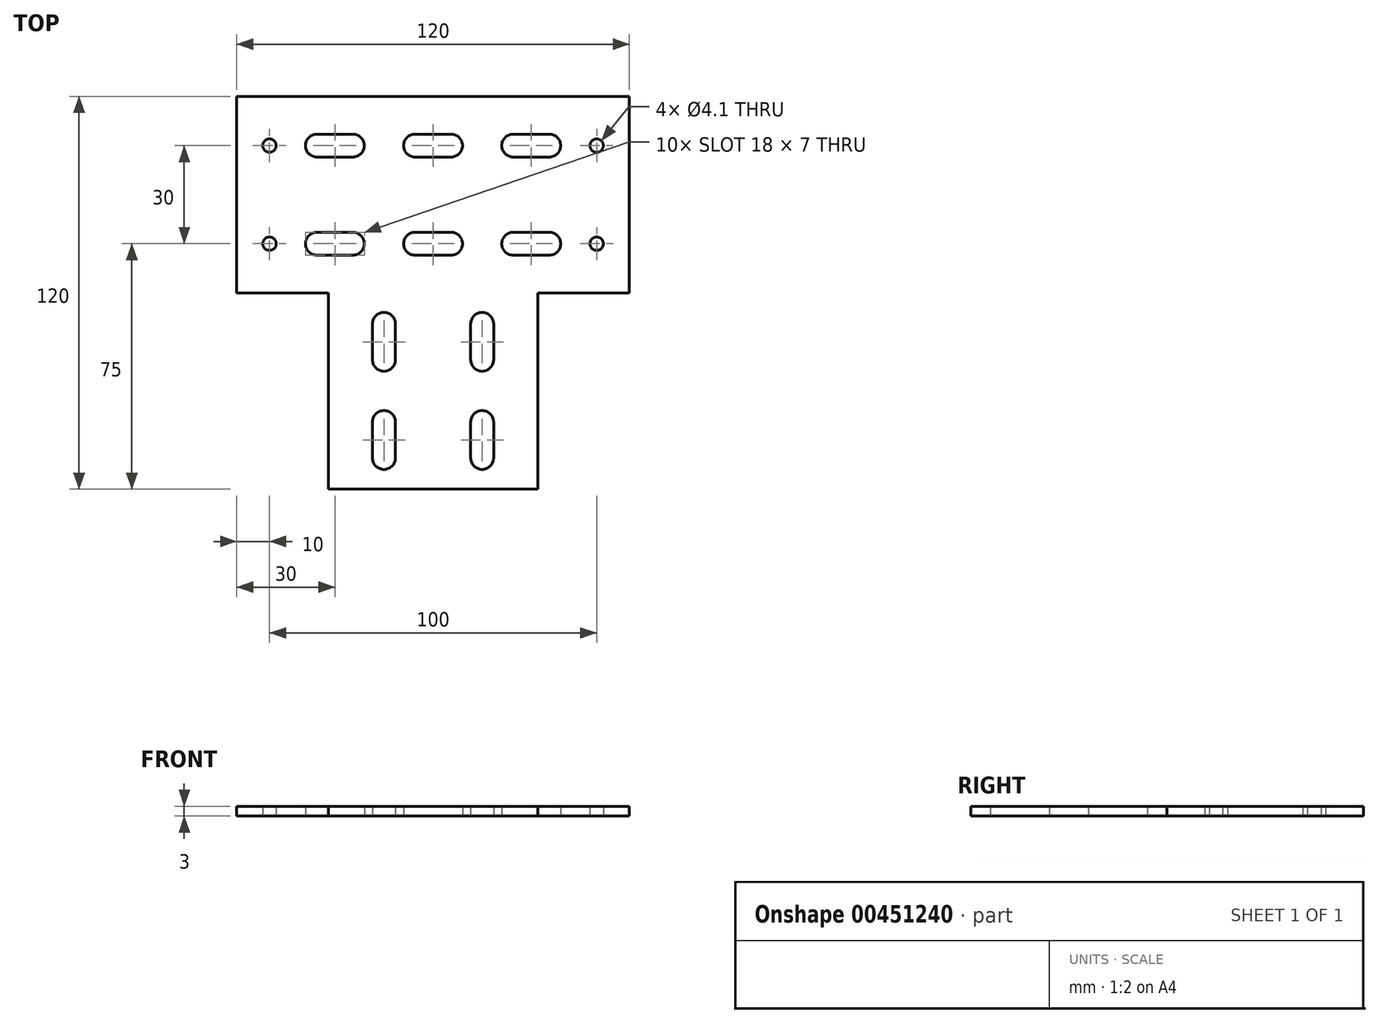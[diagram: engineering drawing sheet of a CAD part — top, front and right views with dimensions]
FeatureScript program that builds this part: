
annotation { "Feature Type Name" : "Feature", "Feature Type Description" : "" }
export const myFeature = defineFeature(function(context is Context, id is Id, definition is map)
    precondition{}
    {
        {
            var Q0;
            Q0=qCreatedBy(makeId("Top.planeOp"),FACE);
            var sketch = newSketch(context, id + "F0", { "sketchPlane" : qUnion([Q0])});
            skLineSegment(sketch, "E0.bottom", {"start": v(32, -60) * mm, "end": v(-32, -60) * mm});
            skLineSegment(sketch, "E0.left", {"start": v(32, -60) * mm, "end": v(32, 0) * mm});
            skLineSegment(sketch, "E0.right", {"start": v(-32, -60) * mm, "end": v(-32, 0) * mm});
            skPoint(sketch, "E0.middle", {"position": v(0, 0) * mm});
            skLineSegment(sketch, "E1", {"start": v(60, 60) * mm, "end": v(60, 0) * mm});
            skLineSegment(sketch, "E2", {"start": v(60, 0) * mm, "end": v(32, 0) * mm});
            skLineSegment(sketch, "E3", {"start": v(-60, 60) * mm, "end": v(-60, 0) * mm});
            skPoint(sketch, "E3.endSnap0", {"position": v(-32, 0) * mm});
            skLineSegment(sketch, "E4", {"start": v(-60, 0) * mm, "end": v(-32, 0) * mm});
            skLineSegment(sketch, "E5", {"start": v(-60, 60) * mm, "end": v(60, 60) * mm});
            skLineSegment(sketch, "E6.bottom", {"start": v(-24.5, 41.5) * mm, "end": v(-35.5, 41.5) * mm});
            skLineSegment(sketch, "E6.top", {"start": v(-24.5, 48.5) * mm, "end": v(-35.5, 48.5) * mm});
            skLineSegment(sketch, "E6.left", {"start": v(-24.5, 41.5) * mm, "end": v(-24.5, 48.5) * mm, "construction": true});
            skLineSegment(sketch, "E6.right", {"start": v(-35.5, 41.5) * mm, "end": v(-35.5, 48.5) * mm, "construction": true});
            skPoint(sketch, "E6.middle", {"position": v(-30, 45) * mm});
            skArc(sketch, "E7", {"start": v(-35.5, 48.5) * mm, "mid": v(-39, 45) * mm, "end": v(-35.5, 41.5) * mm});
            skArc(sketch, "E8", {"start": v(-24.5, 41.5) * mm, "mid": v(-21, 45) * mm, "end": v(-24.5, 48.5) * mm});
            skLineSegment(sketch, "E9.bottom", {"start": v(-11.5, -50.5) * mm, "end": v(-18.5, -50.5) * mm, "construction": true});
            skLineSegment(sketch, "E9.top", {"start": v(-11.5, -39.5) * mm, "end": v(-18.5, -39.5) * mm, "construction": true});
            skLineSegment(sketch, "E9.left", {"start": v(-11.5, -50.5) * mm, "end": v(-11.5, -39.5) * mm});
            skLineSegment(sketch, "E9.right", {"start": v(-18.5, -50.5) * mm, "end": v(-18.5, -39.5) * mm});
            skPoint(sketch, "E9.middle", {"position": v(-15, -45) * mm});
            skLineSegment(sketch, "E10.bottom", {"start": v(11.5, -50.5) * mm, "end": v(18.5, -50.5) * mm, "construction": true});
            skLineSegment(sketch, "E10.top", {"start": v(11.5, -39.5) * mm, "end": v(18.5, -39.5) * mm, "construction": true});
            skLineSegment(sketch, "E10.left", {"start": v(11.5, -50.5) * mm, "end": v(11.5, -39.5) * mm});
            skLineSegment(sketch, "E10.right", {"start": v(18.5, -50.5) * mm, "end": v(18.5, -39.5) * mm});
            skPoint(sketch, "E10.middle", {"position": v(15, -45) * mm});
            skArc(sketch, "E11", {"start": v(-11.5, -39.5) * mm, "mid": v(-15, -36) * mm, "end": v(-18.5, -39.5) * mm});
            skArc(sketch, "E12", {"start": v(-18.5, -50.5) * mm, "mid": v(-15, -54) * mm, "end": v(-11.5, -50.5) * mm});
            skArc(sketch, "E13", {"start": v(18.5, -39.5) * mm, "mid": v(15, -36) * mm, "end": v(11.5, -39.5) * mm});
            skArc(sketch, "E14", {"start": v(11.5, -50.5) * mm, "mid": v(15, -54) * mm, "end": v(18.5, -50.5) * mm});
            skLineSegment(sketch, "E15.bottom", {"start": v(-11.5, -20.5) * mm, "end": v(-18.5, -20.5) * mm, "construction": true});
            skLineSegment(sketch, "E15.top", {"start": v(-11.5, -9.5) * mm, "end": v(-18.5, -9.5) * mm, "construction": true});
            skLineSegment(sketch, "E15.left", {"start": v(-11.5, -20.5) * mm, "end": v(-11.5, -9.5) * mm});
            skLineSegment(sketch, "E15.right", {"start": v(-18.5, -20.5) * mm, "end": v(-18.5, -9.5) * mm});
            skPoint(sketch, "E15.middle", {"position": v(-15, -15) * mm});
            skLineSegment(sketch, "E16.bottom", {"start": v(11.5, -20.5) * mm, "end": v(18.5, -20.5) * mm, "construction": true});
            skLineSegment(sketch, "E16.top", {"start": v(11.5, -9.5) * mm, "end": v(18.5, -9.5) * mm, "construction": true});
            skLineSegment(sketch, "E16.left", {"start": v(11.5, -20.5) * mm, "end": v(11.5, -9.5) * mm});
            skLineSegment(sketch, "E16.right", {"start": v(18.5, -20.5) * mm, "end": v(18.5, -9.5) * mm});
            skPoint(sketch, "E16.middle", {"position": v(15, -15) * mm});
            skArc(sketch, "E17", {"start": v(-11.5, -9.5) * mm, "mid": v(-15, -6) * mm, "end": v(-18.5, -9.5) * mm});
            skArc(sketch, "E18", {"start": v(-18.5, -20.5) * mm, "mid": v(-15, -24) * mm, "end": v(-11.5, -20.5) * mm});
            skArc(sketch, "E19", {"start": v(18.5, -9.5) * mm, "mid": v(15, -6) * mm, "end": v(11.5, -9.5) * mm});
            skArc(sketch, "E20", {"start": v(11.5, -20.5) * mm, "mid": v(15, -24) * mm, "end": v(18.5, -20.5) * mm});
            skLineSegment(sketch, "E21.bottom", {"start": v(35.5, 41.5) * mm, "end": v(24.5, 41.5) * mm});
            skLineSegment(sketch, "E21.top", {"start": v(35.5, 48.5) * mm, "end": v(24.5, 48.5) * mm});
            skLineSegment(sketch, "E21.left", {"start": v(35.5, 41.5) * mm, "end": v(35.5, 48.5) * mm, "construction": true});
            skLineSegment(sketch, "E21.right", {"start": v(24.5, 41.5) * mm, "end": v(24.5, 48.5) * mm, "construction": true});
            skPoint(sketch, "E21.middle", {"position": v(30, 45) * mm});
            skArc(sketch, "E22", {"start": v(24.5, 48.5) * mm, "mid": v(21, 45) * mm, "end": v(24.5, 41.5) * mm});
            skArc(sketch, "E23", {"start": v(35.5, 41.5) * mm, "mid": v(39, 45) * mm, "end": v(35.5, 48.5) * mm});
            skCircle(sketch, "E24", {"center": v(-50, 45) * mm, "radius": 2.05 * mm});
            skCircle(sketch, "E25", {"center": v(50, 45) * mm, "radius": 2.05 * mm});
            skLineSegment(sketch, "E26", {"start": v(-60, 30) * mm, "end": v(-12.13, 30) * mm, "construction": true});
            skLineSegment(sketch, "E27.MirrorCS", {"start": v(-24.5, 18.5) * mm, "end": v(-24.5, 11.5) * mm, "construction": true});
            skLineSegment(sketch, "E28.MirrorCS", {"start": v(-35.5, 18.5) * mm, "end": v(-35.5, 11.5) * mm, "construction": true});
            skLineSegment(sketch, "E29.MirrorCS", {"start": v(24.5, 18.5) * mm, "end": v(24.5, 11.5) * mm, "construction": true});
            skLineSegment(sketch, "E30.MirrorCS", {"start": v(35.5, 18.5) * mm, "end": v(35.5, 11.5) * mm, "construction": true});
            skCircle(sketch, "E31.MirrorC", {"center": v(50, 15) * mm, "radius": 2.05 * mm});
            skPoint(sketch, "E32.MirrorP", {"position": v(-30, 15) * mm});
            skLineSegment(sketch, "E33.MirrorCS", {"start": v(35.5, 11.5) * mm, "end": v(24.5, 11.5) * mm});
            skPoint(sketch, "E34.MirrorP", {"position": v(30, 15) * mm});
            skArc(sketch, "E35.MirrorCS", {"start": v(-24.5, 18.5) * mm, "mid": v(-21, 15) * mm, "end": v(-24.5, 11.5) * mm});
            skLineSegment(sketch, "E36.MirrorCS", {"start": v(35.5, 18.5) * mm, "end": v(24.5, 18.5) * mm});
            skArc(sketch, "E37.MirrorCS", {"start": v(-35.5, 11.5) * mm, "mid": v(-39, 15) * mm, "end": v(-35.5, 18.5) * mm});
            skCircle(sketch, "E38.MirrorC", {"center": v(-50, 15) * mm, "radius": 2.05 * mm});
            skLineSegment(sketch, "E39.MirrorCS", {"start": v(-24.5, 11.5) * mm, "end": v(-35.5, 11.5) * mm});
            skArc(sketch, "E40.MirrorCS", {"start": v(24.5, 11.5) * mm, "mid": v(21, 15) * mm, "end": v(24.5, 18.5) * mm});
            skArc(sketch, "E41.MirrorCS", {"start": v(35.5, 18.5) * mm, "mid": v(39, 15) * mm, "end": v(35.5, 11.5) * mm});
            skLineSegment(sketch, "E42.MirrorCS", {"start": v(-24.5, 18.5) * mm, "end": v(-35.5, 18.5) * mm});
            skLineSegment(sketch, "E43.bottom", {"start": v(5.5, 41.5) * mm, "end": v(-5.5, 41.5) * mm});
            skLineSegment(sketch, "E43.top", {"start": v(5.5, 48.5) * mm, "end": v(-5.5, 48.5) * mm});
            skLineSegment(sketch, "E43.left", {"start": v(5.5, 41.5) * mm, "end": v(5.5, 48.5) * mm, "construction": true});
            skLineSegment(sketch, "E43.right", {"start": v(-5.5, 41.5) * mm, "end": v(-5.5, 48.5) * mm, "construction": true});
            skPoint(sketch, "E43.middle", {"position": v(0, 45) * mm});
            skArc(sketch, "E44", {"start": v(-5.5, 48.5) * mm, "mid": v(-9, 45) * mm, "end": v(-5.5, 41.5) * mm});
            skArc(sketch, "E45", {"start": v(5.5, 41.5) * mm, "mid": v(9, 45) * mm, "end": v(5.5, 48.5) * mm});
            skLineSegment(sketch, "E46.MirrorCS", {"start": v(-5.5, 18.5) * mm, "end": v(-5.5, 11.5) * mm, "construction": true});
            skLineSegment(sketch, "E47.MirrorCS", {"start": v(5.5, 18.5) * mm, "end": v(5.5, 11.5) * mm, "construction": true});
            skLineSegment(sketch, "E48.MirrorCS", {"start": v(5.5, 11.5) * mm, "end": v(-5.5, 11.5) * mm});
            skLineSegment(sketch, "E49.MirrorCS", {"start": v(5.5, 18.5) * mm, "end": v(-5.5, 18.5) * mm});
            skPoint(sketch, "E50.MirrorP", {"position": v(0, 15) * mm});
            skArc(sketch, "E51.MirrorCS", {"start": v(-5.5, 11.5) * mm, "mid": v(-9, 15) * mm, "end": v(-5.5, 18.5) * mm});
            skArc(sketch, "E52.MirrorCS", {"start": v(5.5, 18.5) * mm, "mid": v(9, 15) * mm, "end": v(5.5, 11.5) * mm});
            skSolve(sketch);
        }
        {
            var Q0;
            Q0 = qSketchRegion(id + "F0", true);
            extrude(context, id + "F1", {"entities" : qUnion([Q0]), "depth" : 3 * mm, "offsetDistance" : 25 * mm});
        }
    });
